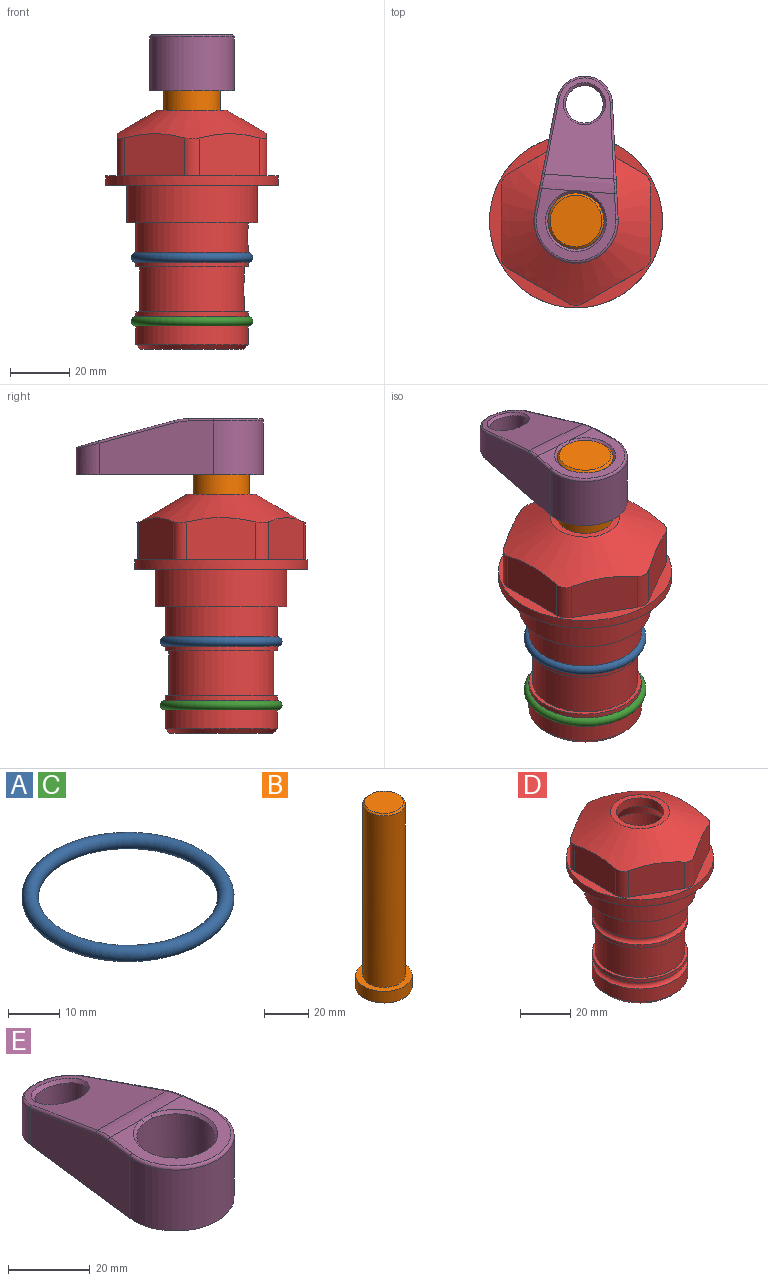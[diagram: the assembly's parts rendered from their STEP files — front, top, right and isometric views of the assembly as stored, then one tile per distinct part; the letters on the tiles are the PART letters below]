
ASSEMBLY  parts=5 mates=4
PART A: 1 faces, bbox 44.7x44.7x3.2 mm
  f0: torus R=19.05mm, axis (0,0,1), area 1193.9mm2
PART B: 6 faces, bbox 25.4x25.4x101.6 mm
  f0: plane 17.46x17.46mm, normal (0,0,1), area 239.5mm2, adj f5
  f1: plane 25.4x25.4mm, normal (0,0,-1), area 506.7mm2, adj f2
  f2: cylinder r=12.7mm len=25.4mm, axis (0,0,1), area 506.7mm2, adj f1,f3
  f3: plane 25.4x25.4mm, normal (0,0,1), area 221.7mm2, adj f2,f4
  f4: cylinder r=9.53mm len=94.46mm, axis (0,0,1), area 5653mm2, adj f3,f5
  f5: cone r=8.73mm half-angle=45deg, axis (0,0,-1), area 64.4mm2, adj f0,f4
PART C: same geometry as A
PART D: 36 faces, bbox 58.7x58.7x81 mm
  f0: cylinder r=17.78mm len=35.56mm, axis (0,0,1), area 1670.8mm2, adj f23,f24,f31
  f1: cylinder r=19.05mm len=38.1mm, axis (0,0,1), area 1191.9mm2, adj f26,f27,f30
  f2: plane 58.66x58.66mm, normal (0,0,-1), area 1150.6mm2, adj f3,f28
  f3: cylinder r=29.33mm len=58.66mm, axis (0,0,-1), area 585.1mm2, adj f2,f4
  f4: plane 58.66x58.66mm, normal (0,0,1), area 475.9mm2, adj f3,f5,f6,f7,f8,f9,f10,f11
  f5: plane 20.32x14.34mm, normal (-0.5,0.87,0), area 324.4mm2, adj f4,f15,f16,f17
  f6: plane 20.32x14.34mm, normal (0.5,0.87,0), area 324.4mm2, adj f4,f14,f15,f17
  f7: plane 23.48x14.34mm, normal (1,0,0), area 324.4mm2, adj f4,f13,f14,f17
  f8: plane 20.32x14.34mm, normal (0.5,-0.87,0), area 324.4mm2, adj f4,f12,f13,f17
  f9: plane 20.32x14.34mm, normal (-0.5,-0.87,0), area 324.4mm2, adj f4,f11,f12,f17
  f10: plane 23.48x14.34mm, normal (-1,0,0), area 324.4mm2, adj f4,f11,f16,f17
  f11: cylinder r=5.08mm len=12.85mm, axis (0,0,-1), area 67.2mm2, adj f4,f9,f10,f17
  f12: cylinder r=5.08mm len=12.85mm, axis (0,0,-1), area 67.2mm2, adj f4,f8,f9,f17
  f13: cylinder r=5.08mm len=12.85mm, axis (0,0,-1), area 67.2mm2, adj f4,f7,f8,f17
  f14: cylinder r=5.08mm len=12.85mm, axis (0,0,-1), area 67.2mm2, adj f4,f6,f7,f17
  f15: cylinder r=5.08mm len=12.85mm, axis (0,0,-1), area 67.2mm2, adj f4,f5,f6,f17
  f16: cylinder r=5.08mm len=12.85mm, axis (0,0,-1), area 67.2mm2, adj f4,f5,f10,f17
  f17: cone r=11.73mm half-angle=60deg, axis (0,0,-1), area 2071.8mm2, adj f5,f6,f7,f8,f9,f10,f11,f12
  f18: plane 23.46x23.46mm, normal (0,0,1), area 147.4mm2, adj f17,f35
  f19: plane 34.93x34.93mm, normal (0,0,-1), area 958mm2, adj f29
  f20: cylinder r=19.05mm len=38.1mm, axis (0,0,1), area 760.1mm2, adj f21,f29
  f21: torus R=19.05mm, axis (0,0,1), area 565.3mm2, adj f20,f22
  f22: cylinder r=19.05mm len=38.1mm, axis (0,0,1), area 190mm2, adj f21,f23
  f23: plane 38.1x38.1mm, normal (0,0,1), area 146.9mm2, adj f0,f22
  f24: plane 38.1x38.1mm, normal (0,0,-1), area 146.9mm2, adj f0,f25
  f25: cylinder r=19.05mm len=38.1mm, axis (0,0,1), area 190mm2, adj f24,f26
  f26: torus R=19.05mm, axis (0,0,1), area 565.3mm2, adj f1,f25
  f27: plane 44.45x44.45mm, normal (0,0,-1), area 411.7mm2, adj f1,f28
  f28: cylinder r=22.23mm len=44.45mm, axis (0,0,1), area 1773.5mm2, adj f2,f27
  f29: cone r=19.05mm half-angle=45deg, axis (0,0,1), area 257.5mm2, adj f19,f20
  f30: cylinder r=3.17mm len=6.75mm, axis (-1,0,0), area 128mm2, adj f1,f33
  f31: cylinder r=3.17mm len=6.35mm, axis (-1,0,0), area 102.5mm2, adj f0,f33
  f32: plane 25.4x25.4mm, normal (0,0,1), area 506.7mm2, adj f33
  f33: cylinder r=12.7mm len=66.42mm, axis (0,0,-1), area 5236.2mm2, adj f30,f31,f32,f34
  f34: cone r=9.53mm half-angle=30deg, axis (0,0,-1), area 443.4mm2, adj f33,f35
  f35: cylinder r=9.53mm len=19.05mm, axis (0,0,-1), area 240.9mm2, adj f18,f34
PART E: 31 faces, bbox 31.7x65.5x19.8 mm
  f0: plane 39.12x18.26mm, normal (0.99,0.12,0), area 612.2mm2, adj f1,f4,f7,f11,f13,f15
  f1: cylinder r=9.53mm len=18.91mm, axis (0,0,-1), area 296.1mm2, adj f0,f2,f7,f17
  f2: plane 39.12x18.26mm, normal (-0.99,0.12,0), area 612.2mm2, adj f1,f4,f7,f12,f14,f16
  f3: cylinder r=6.35mm len=12.7mm, axis (0,0,-1), area 362.4mm2, adj f7,f18
  f4: cylinder r=14.29mm len=28.58mm, axis (0,0,-1), area 882.2mm2, adj f0,f2,f7,f10
  f5: cylinder r=9.53mm len=19.05mm, axis (0,0,-1), area 1092.6mm2, adj f7,f19,f20
  f6: plane 26.99x23.69mm, normal (0,0,1), area 216.2mm2, adj f9,f10,f11,f12,f19
  f7: plane 63.5x28.58mm, normal (0,0,-1), area 661.8mm2, adj f0,f1,f2,f3,f4,f5,f22,f23
  f8: plane 33.52x23.6mm, normal (0,0.26,0.97), area 486mm2, adj f9,f15,f16,f17,f18
  f9: cylinder r=19.05mm len=24.72mm, axis (1,0,0), area 120.4mm2, adj f6,f8,f13,f14,f20
  f10: torus R=13.49mm, axis (0,0,1), area 59mm2, adj f4,f6,f11,f12
  f11: cylinder r=0.79mm len=8.67mm, axis (0.12,-0.99,0), area 10.8mm2, adj f0,f6,f10,f13
  f12: cylinder r=0.79mm len=8.67mm, axis (0.12,0.99,0), area 10.8mm2, adj f2,f6,f10,f14
  f13: bspline ~4.95x1.42mm, area 6.1mm2, adj f0,f9,f11,f15
  f14: bspline ~4.95x1.42mm, area 6.1mm2, adj f2,f9,f12,f16
  f15: cylinder r=0.79mm len=25.95mm, axis (0.12,-0.96,0.26), area 32.9mm2, adj f0,f8,f13,f17
  f16: cylinder r=0.79mm len=25.95mm, axis (0.12,0.96,-0.26), area 32.9mm2, adj f2,f8,f14,f17
  f17: bspline ~18.91x8.38mm, area 30mm2, adj f1,f8,f15,f16
  f18: bspline ~14.29x14.29mm, area 48.3mm2, adj f3,f8
  f19: cone r=9.53mm half-angle=45deg, axis (0,0,1), area 66.5mm2, adj f5,f6,f20
  f20: bspline ~3.22x0.96mm, area 3.5mm2, adj f5,f9,f19
  f21: plane 2.75x2.72mm, normal (0,0,-1), area 2.9mm2, adj f23,f25,f28
  f22: plane 23.05x15.88mm, normal (-0.99,-0.12,0), area 323.6mm2, adj f7,f25,f26,f27,f28,f29
  f23: plane 23.05x15.88mm, normal (0.99,-0.12,0), area 323.6mm2, adj f7,f21,f25,f27,f28,f30
  f24: cylinder r=9.53mm len=10.69mm, axis (0,0,-1), area 114.7mm2, adj f7,f27,f29,f30
  f25: cylinder r=12.7mm len=20.59mm, axis (0,0,-1), area 381.1mm2, adj f7,f21,f22,f23,f26,f28
  f26: plane 2.75x2.72mm, normal (0,0,-1), area 2.9mm2, adj f22,f25,f28
  f27: plane 19.72x18.37mm, normal (0,-0.26,-0.97), area 291.8mm2, adj f22,f23,f24,f28,f29,f30
  f28: cylinder r=15.88mm len=19.92mm, axis (1,0,0), area 54.8mm2, adj f21,f22,f23,f25,f26,f27
  f29: cylinder r=1.59mm len=11mm, axis (0,0,-1), area 34.7mm2, adj f7,f22,f24,f27
  f30: cylinder r=1.59mm len=11mm, axis (0,0,-1), area 34.7mm2, adj f7,f23,f24,f27
PLACE A at identity
PLACE B rot(axis=(0,0,-1),4.1deg) t=(0,0,-12.45)mm
PLACE C t=(0,0,-21.59)mm
PLACE D at identity fixed
PLACE E rot(axis=(0,0,-1),4.1deg) t=(0,0,-12.45)mm
MATE cylindrical B.f2 <-> D.f0  axis (0,0,-1) through (0,0,-50.55)mm
MATE fastened B.f2 <-> E.f4  axis (0,0,1) through (0,0,51.05)mm
MATE fastened D.f0 <-> C.f0  axis (0,0,1) through (0,0,-46.1)mm
MATE fastened A.f0 <-> D.f0  axis (0,0,1) through (0,0,-24.51)mm
